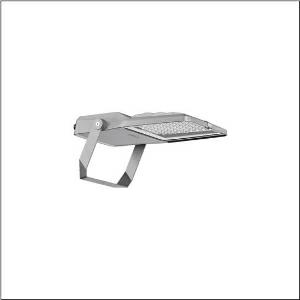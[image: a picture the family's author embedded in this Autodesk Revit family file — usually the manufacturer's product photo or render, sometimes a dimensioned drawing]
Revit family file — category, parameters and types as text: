
# Revit family: floodlight_fl_21_mini___pl64_5xa7772c3e1a_7e86
name_source: partatom
category: Lighting Fixtures
units: mm (PartAtom-declared; Revit-internal decimal feet)

## family parameters
Cut with Voids When Loaded = No
Host = Face
Light Source = No
Part Type = Normal
Room Calculation Point = No
Round Connector Dimension = Use Diameter
Shared = No

## types (1)
- --- (1 x LED, 10150 lm, 87.2 W, 3000K)
    Apparent Load = 87 VA
    CIE Flux Codes = 28 80 98 100 100
    Color Rendering = 80
    Color Temperature = 3000K
    Default Elevation = 1800 mm
    Description = Floodlight FL 21 mini, floodlight, primary light control with lens, of PMMA, primary optical cover: protective disc, of toughened safety glass, transparent, light distribution: PL64, light emission: direct distribution, installation type: surface-mounted, LED, High Power LED, rated luminous flux: 10.150lm, luminous efficacy: 116lm/W, light colour: 830, colour temperature: 3000K, control gear: ECG iQ, control: Street-Remote, Auto-Match, Temp-Guard, Night-Set, Smart-Wire, Desk-Remote (wireless, voltage-free reading and setting of iQ features in the workshop via application-optimized NFC function/RFID function), optimised constant luminous flux control (CLO 2.0), with terminal, 6-pole, mains connection: 220..240V, AC, 50/60Hz, start of lifetime: 87W, end of lifetime: 92W, reduction: 40W, luminaire housing, of diecast aluminium, powder-coated, Siteco® metallic grey (DB 702S), corrosivity category C5 according to DIN EN ISO 12944, mounting bracket, of steel, galvanised, powder-coated, Siteco® metallic grey (DB 702S), protection rating (complete): IP66, insulation class (complete): insulation class II (safety insulation), certification: CE, ENEC, VDE, protection symbol: D, impact resistance: IK08, permissible operating ambient temperature: -40..+40°C, permissible operating ambient temperature for outdoor applications: -40..+50°C, standard: DIN EN 12944, packaging unit: 1 piece

Light Distribution: PL64
    Height = 70 mm
    Lamp = 1 x LED
    Lamp Light Flux = 10150 lm
    Lamp Power = 87.2 W
    Lamp count = 1
    Length = 485 mm
    Luminous efficacy = 116 lm/W
    Manufacturer = Siteco
    ModVariant = No
    Model = 5XA7772C3E1A
    Number of Poles = 1
    OnlyDefault = Yes
    Power Factor = 1
    Product Name = Floodlight FL 21 mini | PL64
    Product group = floodlight | pylon top
    ProductGroupID = 6101
    Protection Class = Protection class II
    Protection Degree = IP 66
    RLX_Detail_Level = 1
    RlxData = <blob elided: 96177 chars, md5=1d181793>
    Socket = socket
    Standby Power = 0 W
    System Light Flux = 10150 lm
    System Power = 87 W
    Type Comments = factory setting: luminous flux: 100 % | dim-lin: 254 | 456 mA
    Type Image = l_1006845.jpg
    URL = http://relux.com
    VarID = @adj_077377
    Voltage = 0 V
    Weight = 0.00 kg
    Width = 337 mm

## geometry (parser evidence)
native form markers: Blend x4, Sweep x10
no freeform markers — native parametric forms only
